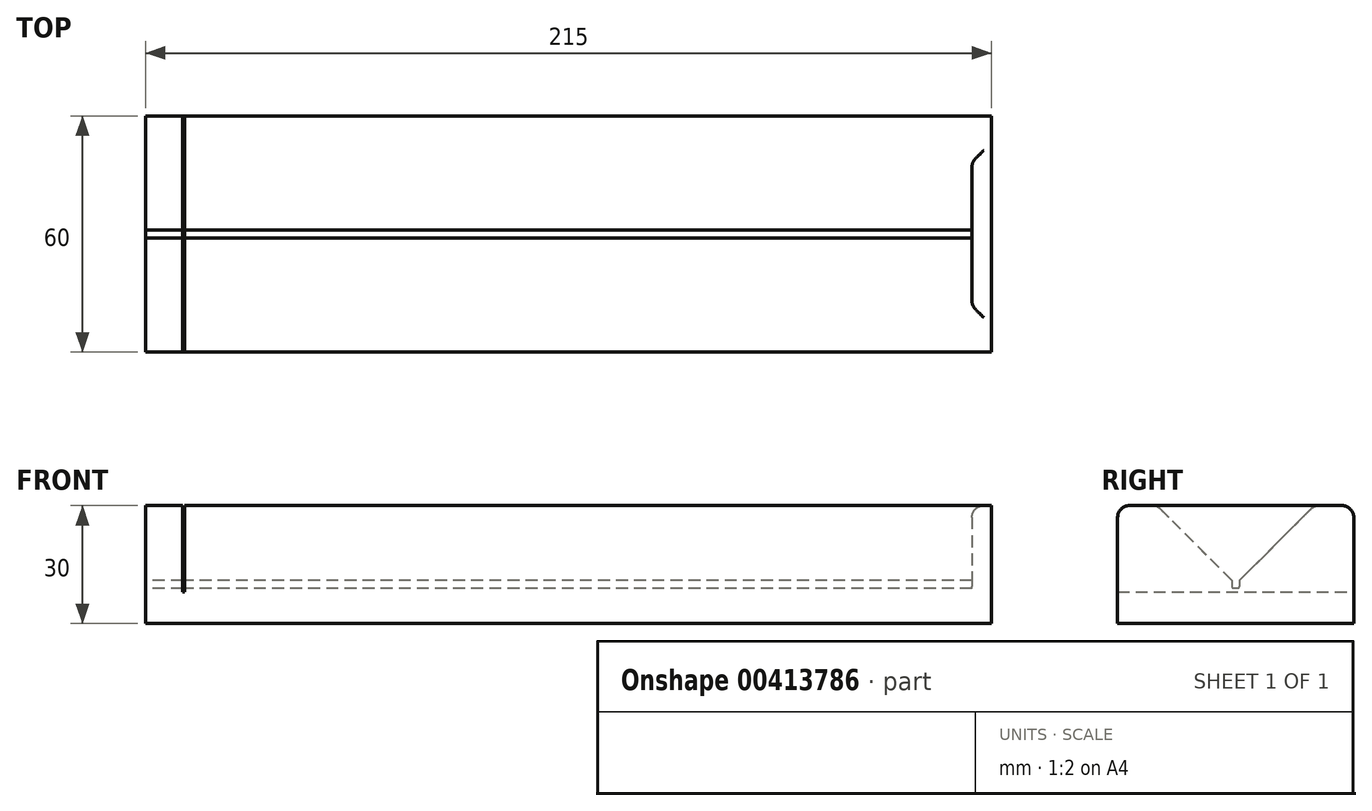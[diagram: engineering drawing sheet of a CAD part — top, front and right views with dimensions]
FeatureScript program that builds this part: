
annotation { "Feature Type Name" : "Feature", "Feature Type Description" : "" }
export const myFeature = defineFeature(function(context is Context, id is Id, definition is map)
    precondition{}
    {
        {
            var Q0;
            Q0=qCreatedBy(makeId("Right.planeOp"),FACE);
            var sketch = newSketch(context, id + "F0", { "sketchPlane" : qUnion([Q0])});
            skLineSegment(sketch, "E0.bottom", {"start": v(30, 30) * mm, "end": v(20, 30) * mm});
            skLineSegment(sketch, "E0.top", {"start": v(30, 0) * mm, "end": v(-30, 0) * mm});
            skLineSegment(sketch, "E0.left", {"start": v(30, 30) * mm, "end": v(30, 0) * mm});
            skLineSegment(sketch, "E0.right", {"start": v(-30, 30) * mm, "end": v(-30, 0) * mm});
            skLineSegment(sketch, "E1", {"start": v(20, 30) * mm, "end": v(1, 11) * mm});
            skLineSegment(sketch, "E2", {"start": v(-1, 11) * mm, "end": v(-20, 30) * mm});
            skLineSegment(sketch, "E3.top", {"start": v(1, 9) * mm, "end": v(-1, 9) * mm});
            skLineSegment(sketch, "E3.left", {"start": v(1, 11) * mm, "end": v(1, 9) * mm});
            skLineSegment(sketch, "E3.right", {"start": v(-1, 11) * mm, "end": v(-1, 9) * mm});
            skPoint(sketch, "E4.orphan", {"position": v(0, 10) * mm});
            skLineSegment(sketch, "E5.trimOffspring", {"start": v(-20, 30) * mm, "end": v(-30, 30) * mm});
            skSolve(sketch);
        }
        {
            var Q0;
            Q0=makeQuery(id+"F0.imprint","IMPRINT",FACE,{"disambiguationData":[TD([[makeQuery(id+"F0.imprint","IMPRINT",EDGE,{"derivedFrom":sQuery(id+"F0.wireOp",EDGE,"E0.bottom")}),1.0]])]});
            extrude(context, id + "F1", {"entities" : qUnion([Q0]), "depth" : 210 * mm});
        }
        {
            var Q0;
            Q0=makeQuery(id+"F1.opExtrude","SWEPT_FACE",FACE,{"disambiguationData":[OSD([sQuery(id+"F0.wireOp",EDGE,"E0.bottom")])]});
            var sketch = newSketch(context, id + "F2", { "sketchPlane" : qUnion([Q0])});
            skLineSegment(sketch, "E6.bottom", {"start": v(10, -48.03) * mm, "end": v(9.5, -48.03) * mm});
            skLineSegment(sketch, "E6.top", {"start": v(10, 50.28) * mm, "end": v(9.5, 50.28) * mm});
            skLineSegment(sketch, "E6.left", {"start": v(10, -48.03) * mm, "end": v(10, 50.28) * mm});
            skLineSegment(sketch, "E6.right", {"start": v(9.5, -48.03) * mm, "end": v(9.5, 50.28) * mm});
            skSolve(sketch);
        }
        {
            var Q0;
            {var subQ0=sQuery(id+"F2.wireOp",EDGE,"E6.left");var subQ1=sQuery(id+"F0.wireOp",EDGE,"E0.bottom");var subQ2=makeQuery(id+"F1.opExtrude","SWEPT_EDGE",EDGE,{"disambiguationData":[OSD([subQ1,sQuery(id+"F0.wireOp",EDGE,"E1")])]});var subQ3=makeQuery(id+"F2.imprint","INTERSECT",VERTEX,{"derivedFrom":[subQ2,subQ0]});Q0=makeQuery(id+"F2.imprint","IMPRINT",FACE,{"disambiguationData":[TD([[makeQuery(id+"F2.imprint","IMPRINT",EDGE,{"disambiguationData":[TD([[subQ3,-1.0]])],"derivedFrom":subQ0}),1.0]])]});}
            var Q1;
            {var subQ0=sQuery(id+"F2.wireOp",EDGE,"E6.bottom");Q1=makeQuery(id+"F2.imprint","IMPRINT",FACE,{"disambiguationData":[TD([[makeQuery(id+"F2.imprint","IMPRINT",EDGE,{"derivedFrom":subQ0}),-1.0]])]});}
            extrude(context, id + "F3", {"entities" : qUnion([Q0, Q1]), "operationType" : NewBodyOperationType.REMOVE, "oppositeDirection" : true, "depth" : 22 * mm});
        }
        {
            var Q0;
            {var subQ0=sQuery(id+"F0.wireOp",EDGE,"E3.right");var subQ1=sQuery(id+"F0.wireOp",EDGE,"E3.top");Q0=makeQuery(id+"F3.boolean.opBoolean","SPLIT",EDGE,{"disambiguationData":[TD([makeQuery(id+"F3.opExtrude","SWEPT_FACE",FACE,{"disambiguationData":[OSD([sQuery(id+"F2.wireOp",EDGE,"E6.left")])]})])],"derivedFrom":makeQuery(id+"F1.opExtrude","SWEPT_EDGE",EDGE,{"disambiguationData":[OSD([subQ1,subQ0])]})});}
            var Q1;
            {var subQ0=sQuery(id+"F0.wireOp",EDGE,"E3.left");var subQ1=sQuery(id+"F0.wireOp",EDGE,"E3.top");Q1=makeQuery(id+"F3.boolean.opBoolean","SPLIT",EDGE,{"disambiguationData":[TD([makeQuery(id+"F3.opExtrude","SWEPT_FACE",FACE,{"disambiguationData":[OSD([sQuery(id+"F2.wireOp",EDGE,"E6.left")])]})])],"derivedFrom":makeQuery(id+"F1.opExtrude","SWEPT_EDGE",EDGE,{"disambiguationData":[OSD([subQ1,subQ0])]})});}
            var Q2;
            {var subQ0=sQuery(id+"F0.wireOp",EDGE,"E3.right");var subQ1=sQuery(id+"F0.wireOp",EDGE,"E3.top");Q2=makeQuery(id+"F3.boolean.opBoolean","SPLIT",EDGE,{"disambiguationData":[TD([makeQuery(id+"F3.opExtrude","SWEPT_FACE",FACE,{"disambiguationData":[OSD([sQuery(id+"F2.wireOp",EDGE,"E6.right")])]})])],"derivedFrom":makeQuery(id+"F1.opExtrude","SWEPT_EDGE",EDGE,{"disambiguationData":[OSD([subQ1,subQ0])]})});}
            var Q3;
            {var subQ0=sQuery(id+"F0.wireOp",EDGE,"E3.left");var subQ1=sQuery(id+"F0.wireOp",EDGE,"E3.top");Q3=makeQuery(id+"F3.boolean.opBoolean","SPLIT",EDGE,{"disambiguationData":[TD([makeQuery(id+"F3.opExtrude","SWEPT_FACE",FACE,{"disambiguationData":[OSD([sQuery(id+"F2.wireOp",EDGE,"E6.right")])]})])],"derivedFrom":makeQuery(id+"F1.opExtrude","SWEPT_EDGE",EDGE,{"disambiguationData":[OSD([subQ1,subQ0])]})});}
            fillet(context, id + "F4", {"entities" : qUnion([Q0, Q1, Q2, Q3]), "radius" : .5 * mm, "tangentPropagation" : true, "allowEdgeOverflow" : false});
        }
        {
            var Q0;
            Q0=makeQuery(id+"F1.opExtrude","CAP_FACE",FACE,{"disambiguationData":[OSD([sQuery(id+"F0.wireOp",EDGE,"E0.bottom"),sQuery(id+"F0.wireOp",EDGE,"E0.top"),sQuery(id+"F0.wireOp",EDGE,"E0.left"),sQuery(id+"F0.wireOp",EDGE,"E0.right"),sQuery(id+"F0.wireOp",EDGE,"E1"),sQuery(id+"F0.wireOp",EDGE,"E2"),sQuery(id+"F0.wireOp",EDGE,"E3.top"),sQuery(id+"F0.wireOp",EDGE,"E3.left"),sQuery(id+"F0.wireOp",EDGE,"E3.right"),sQuery(id+"F0.wireOp",EDGE,"E5.trimOffspring")])],"isStart":false});
            var sketch = newSketch(context, id + "F5", { "sketchPlane" : qUnion([Q0])});
            skLineSegment(sketch, "E7.bottom", {"start": v(-30, 0) * mm, "end": v(30, 0) * mm});
            skLineSegment(sketch, "E7.top", {"start": v(-30, 30) * mm, "end": v(30, 30) * mm});
            skLineSegment(sketch, "E7.left", {"start": v(-30, 0) * mm, "end": v(-30, 30) * mm});
            skLineSegment(sketch, "E7.right", {"start": v(30, 0) * mm, "end": v(30, 30) * mm});
            skSolve(sketch);
        }
        {
            var Q0;
            {var subQ5=sQuery(id+"F0.wireOp",EDGE,"E1");Q0=makeQuery(id+"F5.imprint","IMPRINT",FACE,{"disambiguationData":[TD([[makeQuery(id+"F5.imprint","IMPRINT",EDGE,{"derivedFrom":makeQuery(id+"F1.opExtrude","CAP_EDGE",EDGE,{"disambiguationData":[OSD([subQ5])],"isStart":false})}),-1.0]])]});}
            var Q1;
            {var subQ16=sQuery(id+"F5.wireOp",EDGE,"E7.bottom");Q1=makeQuery(id+"F5.imprint","IMPRINT",FACE,{"disambiguationData":[TD([[makeQuery(id+"F5.imprint","IMPRINT",EDGE,{"derivedFrom":subQ16}),-1.0]])]});}
            extrude(context, id + "F6", {"entities" : qUnion([Q0, Q1]), "operationType" : NewBodyOperationType.ADD, "depth" : 5 * mm});
        }
        {
            var Q0;
            {var subQ0=sQuery(id+"F0.wireOp",EDGE,"E0.bottom");var subQ1=sQuery(id+"F0.wireOp",EDGE,"E0.left");Q0=makeQuery(id+"F3.boolean.opBoolean","SPLIT",EDGE,{"disambiguationData":[TD([makeQuery(id+"F3.opExtrude","SWEPT_FACE",FACE,{"disambiguationData":[OSD([sQuery(id+"F2.wireOp",EDGE,"E6.left")])]})])],"derivedFrom":makeQuery(id+"F1.opExtrude","SWEPT_EDGE",EDGE,{"disambiguationData":[OSD([subQ0,subQ1])]})});}
            var Q1;
            {var subQ0=sQuery(id+"F0.wireOp",EDGE,"E0.bottom");var subQ1=sQuery(id+"F0.wireOp",EDGE,"E0.left");Q1=makeQuery(id+"F3.boolean.opBoolean","SPLIT",EDGE,{"disambiguationData":[TD([makeQuery(id+"F3.opExtrude","SWEPT_FACE",FACE,{"disambiguationData":[OSD([sQuery(id+"F2.wireOp",EDGE,"E6.right")])]})])],"derivedFrom":makeQuery(id+"F1.opExtrude","SWEPT_EDGE",EDGE,{"disambiguationData":[OSD([subQ0,subQ1])]})});}
            var Q2;
            {var subQ0=sQuery(id+"F0.wireOp",EDGE,"E5.trimOffspring");var subQ1=sQuery(id+"F0.wireOp",EDGE,"E0.right");Q2=makeQuery(id+"F3.boolean.opBoolean","SPLIT",EDGE,{"disambiguationData":[TD([makeQuery(id+"F3.opExtrude","SWEPT_FACE",FACE,{"disambiguationData":[OSD([sQuery(id+"F2.wireOp",EDGE,"E6.left")])]})])],"derivedFrom":makeQuery(id+"F1.opExtrude","SWEPT_EDGE",EDGE,{"disambiguationData":[OSD([subQ1,subQ0])]})});}
            var Q3;
            {var subQ0=sQuery(id+"F0.wireOp",EDGE,"E5.trimOffspring");var subQ1=sQuery(id+"F0.wireOp",EDGE,"E0.right");Q3=makeQuery(id+"F3.boolean.opBoolean","SPLIT",EDGE,{"disambiguationData":[TD([makeQuery(id+"F3.opExtrude","SWEPT_FACE",FACE,{"disambiguationData":[OSD([sQuery(id+"F2.wireOp",EDGE,"E6.right")])]})])],"derivedFrom":makeQuery(id+"F1.opExtrude","SWEPT_EDGE",EDGE,{"disambiguationData":[OSD([subQ1,subQ0])]})});}
            var Q4;
            {var subQ0=sQuery(id+"F0.wireOp",EDGE,"E5.trimOffspring");var subQ1=sQuery(id+"F0.wireOp",EDGE,"E2");Q4=makeQuery(id+"F3.boolean.opBoolean","SPLIT",EDGE,{"disambiguationData":[TD([makeQuery(id+"F3.opExtrude","SWEPT_FACE",FACE,{"disambiguationData":[OSD([sQuery(id+"F2.wireOp",EDGE,"E6.left")])]})])],"derivedFrom":makeQuery(id+"F1.opExtrude","SWEPT_EDGE",EDGE,{"disambiguationData":[OSD([subQ1,subQ0])]})});}
            var Q5;
            {var subQ0=sQuery(id+"F0.wireOp",EDGE,"E5.trimOffspring");var subQ1=sQuery(id+"F0.wireOp",EDGE,"E2");Q5=makeQuery(id+"F3.boolean.opBoolean","SPLIT",EDGE,{"disambiguationData":[TD([makeQuery(id+"F3.opExtrude","SWEPT_FACE",FACE,{"disambiguationData":[OSD([sQuery(id+"F2.wireOp",EDGE,"E6.right")])]})])],"derivedFrom":makeQuery(id+"F1.opExtrude","SWEPT_EDGE",EDGE,{"disambiguationData":[OSD([subQ1,subQ0])]})});}
            var Q6;
            {var subQ0=sQuery(id+"F0.wireOp",EDGE,"E0.bottom");var subQ1=sQuery(id+"F0.wireOp",EDGE,"E1");Q6=makeQuery(id+"F3.boolean.opBoolean","SPLIT",EDGE,{"disambiguationData":[TD([makeQuery(id+"F3.opExtrude","SWEPT_FACE",FACE,{"disambiguationData":[OSD([sQuery(id+"F2.wireOp",EDGE,"E6.right")])]})])],"derivedFrom":makeQuery(id+"F1.opExtrude","SWEPT_EDGE",EDGE,{"disambiguationData":[OSD([subQ0,subQ1])]})});}
            var Q7;
            {var subQ0=sQuery(id+"F0.wireOp",EDGE,"E0.bottom");var subQ1=sQuery(id+"F0.wireOp",EDGE,"E1");Q7=makeQuery(id+"F3.boolean.opBoolean","SPLIT",EDGE,{"disambiguationData":[TD([makeQuery(id+"F3.opExtrude","SWEPT_FACE",FACE,{"disambiguationData":[OSD([sQuery(id+"F2.wireOp",EDGE,"E6.left")])]})])],"derivedFrom":makeQuery(id+"F1.opExtrude","SWEPT_EDGE",EDGE,{"disambiguationData":[OSD([subQ0,subQ1])]})});}
            var Q8;
            Q8=makeQuery(id+"F6.opExtrude","CAP_EDGE",EDGE,{"disambiguationData":[OSD([sQuery(id+"F5.wireOp",EDGE,"E7.top")])],"isStart":true});
            fillet(context, id + "F7", {"entities" : qUnion([Q0, Q1, Q2, Q3, Q4, Q5, Q6, Q7, Q8]), "radius" : 3 * mm, "tangentPropagation" : true, "allowEdgeOverflow" : false});
        }
    });
